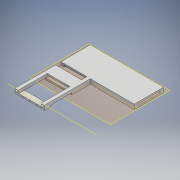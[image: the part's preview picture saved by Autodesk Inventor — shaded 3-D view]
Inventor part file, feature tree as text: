
AUTODESK INVENTOR PART (.ipt)
format: ipt  version: 2018 (Build 220112000, 112)  size: 285,696 bytes
history: native  units: mm
features: extrude x11, sketch x7, plane x3, other x2, mirror x2, projected_geometry x1
ambient origin geometry x8: Origin, YZ Plane, XZ Plane, XY Plane, X Axis, Y Axis, Z Axis, Center Point
bodies: Body1 (feature_tree)
feature tree (26):
  other  "Sólido1"
  sketch  "Boceto1"  dims[d7=5.0mm d9=2.5mm d10=0.0mm]
  extrude  "Extrusión1"  Depth=2.5mm TaperAngle=0.0deg
  extrude  "Extrusión2"  Depth=5.0mm
  plane  "Plano de trabajo3"
  mirror  "Simetría3"
  extrude  "Extrusión11"  Depth=5.0mm
  sketch  "Boceto7"  dims[d69=33.5mm d74=5.0mm]
  plane  "Plano de trabajo4"
  extrude  "Extrusión12"  Depth=5.0mm
  extrude  "Extrusión13"  Depth=8.0mm
  extrude  "Extrusión14"  Depth=42.4mm
  mirror  "Simetría4"
  extrude  "Extrusión15"  Depth=2.5mm TaperAngle=0.0deg
  sketch  "Boceto9"  dims[d77=70.0mm d78=8.0mm]
  other  "Eje de trabajo2"
  extrude  "Extrusión16"  TaperAngle=120.0deg  [1 undecoded]
  plane  "Plano de trabajo5"
  extrude  "Extrusión17"  Depth=5.0mm TaperAngle=0.0deg
  sketch  "Boceto11"  dims[d82=173.0mm d86=21.75mm d87=0.0mm d88=120.0deg d89=5.0mm d90=0.0mm d92=21.75mm d93=0.0mm d94=5.0mm d95=20.5mm d96=5.0mm d97=5.0mm d98=5.0mm d99=5.0mm d100=5.0mm d101=22.0mm d102=22.38mm d103=23.0mm d104=24.38mm d105=25.5mm d106=21.75mm d107=0.0mm d108=5.0mm d109=2.5mm d110=40.0mm d111=30.0mm d112=31.5mm d113=21.75mm d114=0.0mm d115=10.0mm d116=0.0mm d117=2.5mm d118=2.5mm d119=38.5mm d120=1.5mm d121=1.5mm d122=1.5mm d123=10.0mm d124=10.0mm d125=12.0mm d126=2.5mm d127=0.0mm d128=2.5mm d129=0.0mm]
  extrude  "Extrusión18"  Depth=2.5mm TaperAngle=0.0deg
  extrude  "Extrusión19"  Depth=5.0mm
  sketch  "Boceto6"  dims[d11=1.0mm d12=0.0mm d68=5.0mm]
  sketch  "Boceto8"  dims[d75=33.5mm d76=5.0mm]
  sketch  "Boceto10"  dims[d79=4.5mm d80=0.0mm d81=42.4mm]
  projected_geometry  "Contorno proyectado2"
note: 1 required parameter value undecoded (feature->parameter linkage not recoverable at this tier; creation-order binding heuristic only, values carry confidence <= 0.55)
